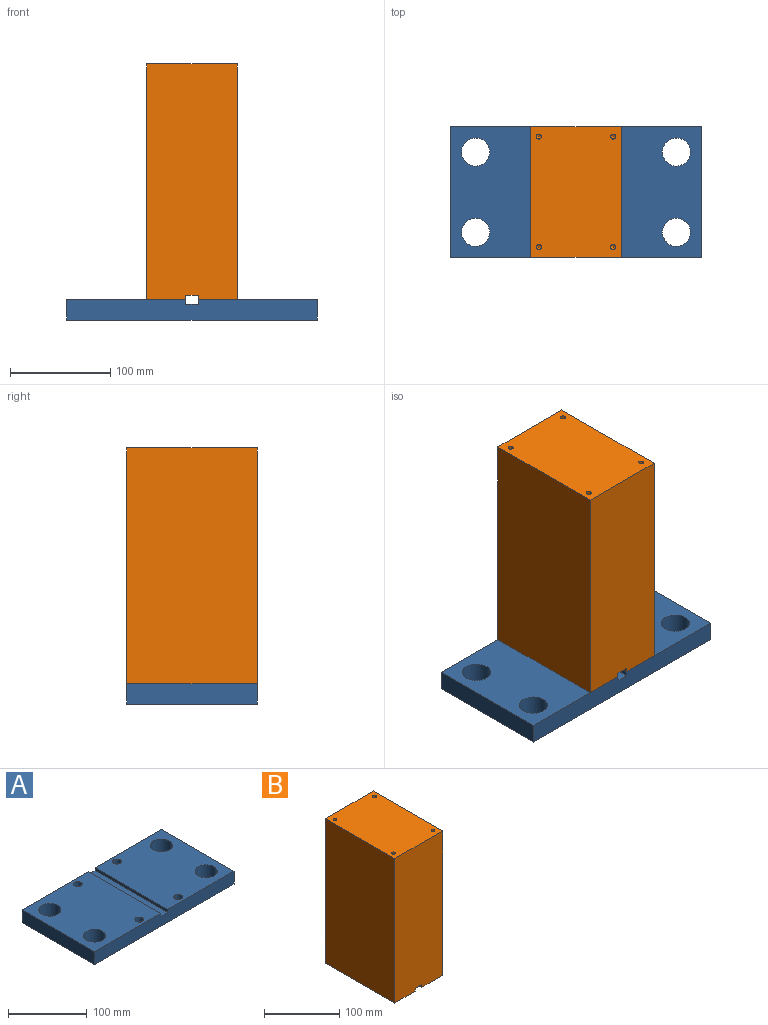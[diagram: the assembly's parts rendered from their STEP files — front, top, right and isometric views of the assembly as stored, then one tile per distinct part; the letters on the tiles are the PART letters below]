
ASSEMBLY  parts=2 mates=1
PART A: 26 faces, bbox 250x130x20 mm
  f0: plane 130x119mm, normal (0,0,1), area 14048.4mm2, adj f2,f3,f4,f7,f16,f19,f22,f23
  f1: plane 130x119mm, normal (0,0,1), area 14048.4mm2, adj f2,f4,f5,f10,f13,f20,f21,f24
  f2: plane 250x20mm, normal (0,1,0), area 4946mm2, adj f0,f1,f3,f5,f6,f23,f24,f25
  f3: plane 130x20mm, normal (-1,0,0), area 2600mm2, adj f0,f2,f4,f6
  f4: plane 250x20mm, normal (0,-1,0), area 4946mm2, adj f0,f1,f3,f5,f6,f23,f24,f25
  f5: plane 130x20mm, normal (1,0,0), area 2600mm2, adj f1,f2,f4,f6
  f6: plane 250x130mm, normal (0,0,-1), area 29102.2mm2, adj f2,f3,f4,f5,f9,f12,f15,f18
  f7: cylinder r=5.5mm len=11mm, axis (0,0,-1), area 345.6mm2, adj f0,f8
  f8: plane 17.25x17.25mm, normal (0,0,-1), area 138.7mm2, adj f7,f9
  f9: cylinder r=8.62mm len=17.25mm, axis (0,0,-1), area 541.9mm2, adj f6,f8
  f10: cylinder r=5.5mm len=11mm, axis (0,0,-1), area 345.6mm2, adj f1,f11
  f11: plane 17.25x17.25mm, normal (0,0,-1), area 138.7mm2, adj f10,f12
  f12: cylinder r=8.62mm len=17.25mm, axis (0,0,-1), area 541.9mm2, adj f6,f11
  f13: cylinder r=5.5mm len=11mm, axis (0,0,-1), area 345.6mm2, adj f1,f14
  f14: plane 17.25x17.25mm, normal (0,0,-1), area 138.7mm2, adj f13,f15
  f15: cylinder r=8.62mm len=17.25mm, axis (0,0,-1), area 541.9mm2, adj f6,f14
  f16: cylinder r=5.5mm len=11mm, axis (0,0,-1), area 345.6mm2, adj f0,f17
  f17: plane 17.25x17.25mm, normal (0,0,-1), area 138.7mm2, adj f16,f18
  f18: cylinder r=8.62mm len=17.25mm, axis (0,0,-1), area 541.9mm2, adj f6,f17
  f19: cylinder r=14mm len=28mm, axis (0,0,-1), area 1759.3mm2, adj f0,f6
  f20: cylinder r=14mm len=28mm, axis (0,0,-1), area 1759.3mm2, adj f1,f6
  f21: cylinder r=14mm len=28mm, axis (0,0,-1), area 1759.3mm2, adj f1,f6
  f22: cylinder r=14mm len=28mm, axis (0,0,-1), area 1759.3mm2, adj f0,f6
  f23: plane 130x4.5mm, normal (1,0,0), area 585mm2, adj f0,f2,f4,f25
  f24: plane 130x4.5mm, normal (-1,0,0), area 585mm2, adj f1,f2,f4,f25
  f25: plane 130x12mm, normal (0,0,1), area 1560mm2, adj f2,f4,f23,f24
PART B: 26 faces, bbox 90x130x235 mm
  f0: plane 130x39mm, normal (0,0,-1), area 4942.8mm2, adj f1,f2,f3,f16,f20,f23
  f1: plane 235x90mm, normal (0,-1,0), area 21096mm2, adj f0,f3,f4,f5,f6,f23,f24,f25
  f2: plane 235x90mm, normal (0,1,0), area 21096mm2, adj f0,f3,f4,f5,f6,f23,f24,f25
  f3: plane 235x130mm, normal (-1,0,0), area 30550mm2, adj f0,f1,f2,f6
  f4: plane 235x130mm, normal (1,0,0), area 30550mm2, adj f1,f2,f5,f6
  f5: plane 130x39mm, normal (0,0,-1), area 4942.8mm2, adj f1,f2,f4,f18,f22,f24
  f6: plane 130x90mm, normal (0,0,1), area 11621.5mm2, adj f1,f2,f3,f4,f8,f10,f12,f14
  f7: cone r=0mm half-angle=59deg, axis (0,0,1), area 22.9mm2, adj f8
  f8: cylinder r=2.5mm len=27mm, axis (0,0,1), area 424.1mm2, adj f6,f7
  f9: cone r=0mm half-angle=59deg, axis (0,0,1), area 22.9mm2, adj f10
  f10: cylinder r=2.5mm len=27mm, axis (0,0,1), area 424.1mm2, adj f6,f9
  f11: cone r=0mm half-angle=59deg, axis (0,0,1), area 22.9mm2, adj f12
  f12: cylinder r=2.5mm len=27mm, axis (0,0,1), area 424.1mm2, adj f6,f11
  f13: cone r=0mm half-angle=59deg, axis (0,0,1), area 22.9mm2, adj f14
  f14: cylinder r=2.5mm len=27mm, axis (0,0,1), area 424.1mm2, adj f6,f13
  f15: cone r=0mm half-angle=59deg, axis (0,0,-1), area 74.2mm2, adj f16
  f16: cylinder r=4.5mm len=27mm, axis (0,0,-1), area 763.4mm2, adj f0,f15
  f17: cone r=0mm half-angle=59deg, axis (0,0,-1), area 74.2mm2, adj f18
  f18: cylinder r=4.5mm len=27mm, axis (0,0,-1), area 763.4mm2, adj f5,f17
  f19: cone r=0mm half-angle=59deg, axis (0,0,-1), area 74.2mm2, adj f20
  f20: cylinder r=4.5mm len=27mm, axis (0,0,-1), area 763.4mm2, adj f0,f19
  f21: cone r=0mm half-angle=59deg, axis (0,0,-1), area 74.2mm2, adj f22
  f22: cylinder r=4.5mm len=27mm, axis (0,0,-1), area 763.4mm2, adj f5,f21
  f23: plane 130x4.5mm, normal (1,0,0), area 585mm2, adj f0,f1,f2,f25
  f24: plane 130x4.5mm, normal (-1,0,0), area 585mm2, adj f1,f2,f5,f25
  f25: plane 130x12mm, normal (0,0,-1), area 1560mm2, adj f1,f2,f23,f24
PLACE A t=(-46.09,194.61,69.81)mm
PLACE B t=(-46.09,194.61,324.81)mm
MATE pin_slot A.f16 <-> B.f19  axis (0,0,1) through (-81.09,139.61,89.81)mm
